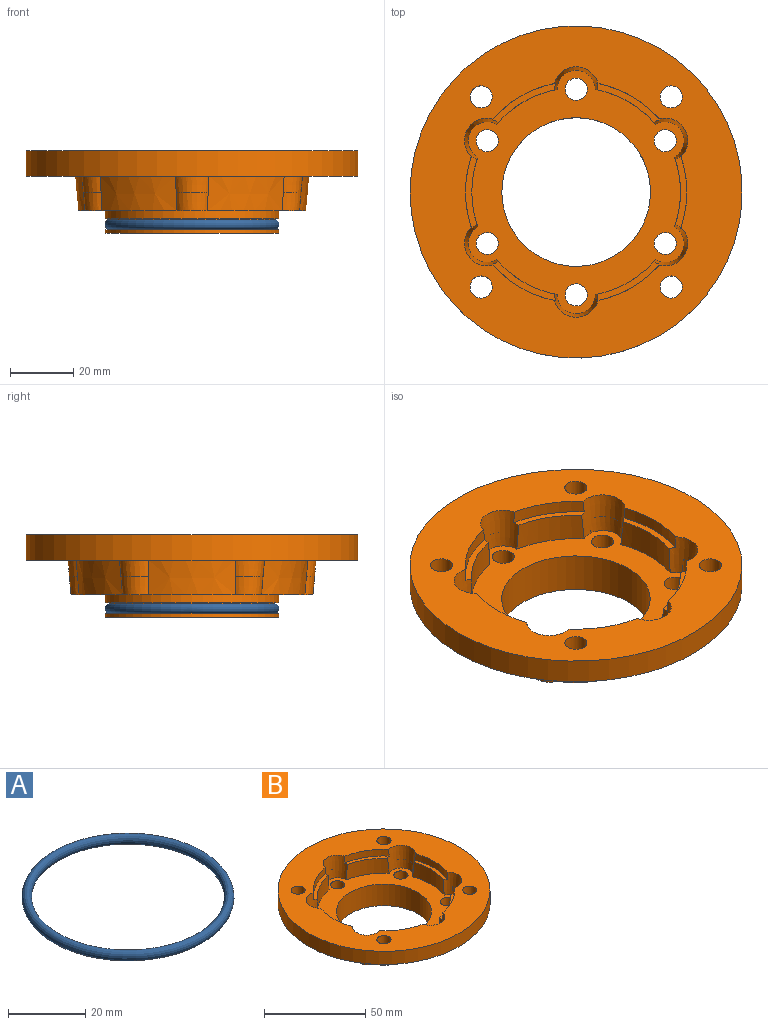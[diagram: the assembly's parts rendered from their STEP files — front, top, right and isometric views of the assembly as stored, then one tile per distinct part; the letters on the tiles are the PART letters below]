
ASSEMBLY  parts=2 mates=1
PART A: 1 faces, bbox 55x55x3 mm
  f0: revolved ~55x55mm, area 1427.9mm2
PART B: 58 faces, bbox 105x105x26 mm
  f0: cylinder r=33mm len=19.1mm, axis (0,0,-1), area 195.2mm2, adj f4,f30,f41,f56
  f1: cylinder r=33mm len=22.06mm, axis (0,0,-1), area 195.2mm2, adj f8,f30,f53,f56
  f2: cylinder r=35mm len=23.1mm, axis (0,0,-1), area 92.6mm2, adj f8,f32,f53,f56
  f3: cylinder r=35mm len=20mm, axis (0,0,-1), area 92.6mm2, adj f4,f32,f41,f56
  f4: plane 20x12.36mm, normal (0,0,1), area 44.2mm2, adj f0,f3,f41,f56
  f5: cone r=37mm half-angle=5.2deg, axis (0,0,1), area 310.4mm2, adj f34,f36,f40,f55
  f6: cylinder r=33mm len=19.1mm, axis (0,0,-1), area 195.2mm2, adj f12,f30,f50,f53
  f7: cylinder r=35mm len=20mm, axis (0,0,-1), area 92.6mm2, adj f12,f32,f50,f53
  f8: plane 23.1x3.64mm, normal (0,0,1), area 44.2mm2, adj f1,f2,f53,f56
  f9: cone r=37mm half-angle=5.2deg, axis (0,0,1), area 310.4mm2, adj f34,f36,f52,f55
  f10: cylinder r=33mm len=19.1mm, axis (0,0,-1), area 195.2mm2, adj f30,f31,f47,f50
  f11: cylinder r=35mm len=20mm, axis (0,0,-1), area 92.6mm2, adj f31,f32,f47,f50
  f12: plane 20x12.36mm, normal (0,0,1), area 44.2mm2, adj f6,f7,f50,f53
  f13: cone r=37mm half-angle=5.2deg, axis (0,0,1), area 310.4mm2, adj f34,f36,f49,f52
  f14: cylinder r=33mm len=22.06mm, axis (0,0,-1), area 195.2mm2, adj f16,f30,f44,f47
  f15: cylinder r=35mm len=23.1mm, axis (0,0,-1), area 92.6mm2, adj f16,f32,f44,f47
  f16: plane 23.1x3.64mm, normal (0,0,1), area 44.2mm2, adj f14,f15,f44,f47
  f17: cone r=37mm half-angle=5.2deg, axis (0,0,1), area 310.4mm2, adj f34,f36,f46,f49
  f18: cylinder r=33mm len=19.1mm, axis (0,0,-1), area 195.2mm2, adj f20,f30,f41,f44
  f19: cylinder r=35mm len=20mm, axis (0,0,-1), area 92.6mm2, adj f20,f32,f41,f44
  f20: plane 20x12.36mm, normal (0,0,1), area 44.2mm2, adj f18,f19,f41,f44
  f21: cone r=37mm half-angle=5.2deg, axis (0,0,1), area 310.4mm2, adj f34,f36,f43,f46
  f22: cylinder r=3.5mm len=8mm, axis (0,0,1), area 175.9mm2, adj f32,f34
  f23: cylinder r=3.5mm len=8mm, axis (0,0,1), area 175.9mm2, adj f32,f34
  f24: cylinder r=3.5mm len=8mm, axis (0,0,1), area 175.9mm2, adj f32,f34
  f25: cylinder r=25mm len=50mm, axis (0,0,-1), area 549.8mm2, adj f26,f38
  f26: plane 55x55mm, normal (0,0,1), area 412.3mm2, adj f25,f27
  f27: cylinder r=27.5mm len=55mm, axis (0,0,-1), area 172.8mm2, adj f26,f28
  f28: plane 55x55mm, normal (0,0,-1), area 640.9mm2, adj f27,f29
  f29: cylinder r=23.5mm len=47mm, axis (0,0,-1), area 1919.5mm2, adj f28,f30
  f30: plane 77x68.29mm, normal (0,0,1), area 1771.8mm2, adj f0,f1,f6,f10,f14,f18,f29,f41
  f31: plane 20x12.36mm, normal (0,0,1), area 44.2mm2, adj f10,f11,f47,f50
  f32: plane 105x105mm, normal (0,0,1), area 4368.1mm2, adj f2,f3,f7,f11,f15,f19,f22,f23
  f33: cylinder r=52.5mm len=105mm, axis (0,0,-1), area 2638.9mm2, adj f32,f34
  f34: plane 105x105mm, normal (0,0,-1), area 4105.3mm2, adj f5,f9,f13,f17,f21,f22,f23,f24
  f35: cone r=37mm half-angle=5.2deg, axis (0,0,1), area 310.4mm2, adj f34,f36,f40,f43
  f36: plane 76.5x72mm, normal (0,0,-1), area 1556.4mm2, adj f5,f9,f13,f17,f21,f35,f37,f40
  f37: cylinder r=27.5mm len=55mm, axis (0,0,-1), area 432mm2, adj f36,f38
  f38: plane 55x55mm, normal (0,0,-1), area 412.3mm2, adj f25,f37
  f39: cylinder r=3.5mm len=8mm, axis (0,0,1), area 175.9mm2, adj f32,f34
  f40: cone r=5.75mm half-angle=5deg, axis (0,0,1), area 130mm2, adj f5,f34,f35,f36
  f41: cone r=6mm half-angle=5deg, axis (0,0,1), area 256.5mm2, adj f0,f3,f4,f18,f19,f20,f30,f32
  f42: cylinder r=3.5mm len=7mm, axis (0,0,-1), area 131.9mm2, adj f30,f36
  f43: cone r=5.75mm half-angle=5deg, axis (0,0,1), area 130mm2, adj f21,f34,f35,f36
  f44: cone r=6mm half-angle=5deg, axis (0,0,1), area 256.5mm2, adj f14,f15,f16,f18,f19,f20,f30,f32
  f45: cylinder r=3.5mm len=7mm, axis (0,0,-1), area 131.9mm2, adj f30,f36
  f46: cone r=5.75mm half-angle=5deg, axis (0,0,1), area 130mm2, adj f17,f21,f34,f36
  f47: cone r=6mm half-angle=5deg, axis (0,0,1), area 256.5mm2, adj f10,f11,f14,f15,f16,f30,f31,f32
  f48: cylinder r=3.5mm len=7mm, axis (0,0,-1), area 131.9mm2, adj f30,f36
  f49: cone r=5.75mm half-angle=5deg, axis (0,0,1), area 130mm2, adj f13,f17,f34,f36
  f50: cone r=6mm half-angle=5deg, axis (0,0,1), area 256.5mm2, adj f6,f7,f10,f11,f12,f30,f31,f32
  f51: cylinder r=3.5mm len=7mm, axis (0,0,-1), area 131.9mm2, adj f30,f36
  f52: cone r=5.75mm half-angle=5deg, axis (0,0,1), area 130mm2, adj f9,f13,f34,f36
  f53: cone r=6mm half-angle=5deg, axis (0,0,1), area 256.5mm2, adj f1,f2,f6,f7,f8,f12,f30,f32
  f54: cylinder r=3.5mm len=7mm, axis (0,0,-1), area 131.9mm2, adj f30,f36
  f55: cone r=5.75mm half-angle=5deg, axis (0,0,1), area 130mm2, adj f5,f9,f34,f36
  f56: cone r=6mm half-angle=5deg, axis (0,0,1), area 256.5mm2, adj f0,f1,f2,f3,f4,f8,f30,f32
  f57: cylinder r=3.5mm len=7mm, axis (0,0,-1), area 131.9mm2, adj f30,f36
PLACE A at identity
PLACE B at identity fixed
MATE revolute B.f0 <-> A.f0  axis (0,0,1) through (0,0,-4.25)mm
